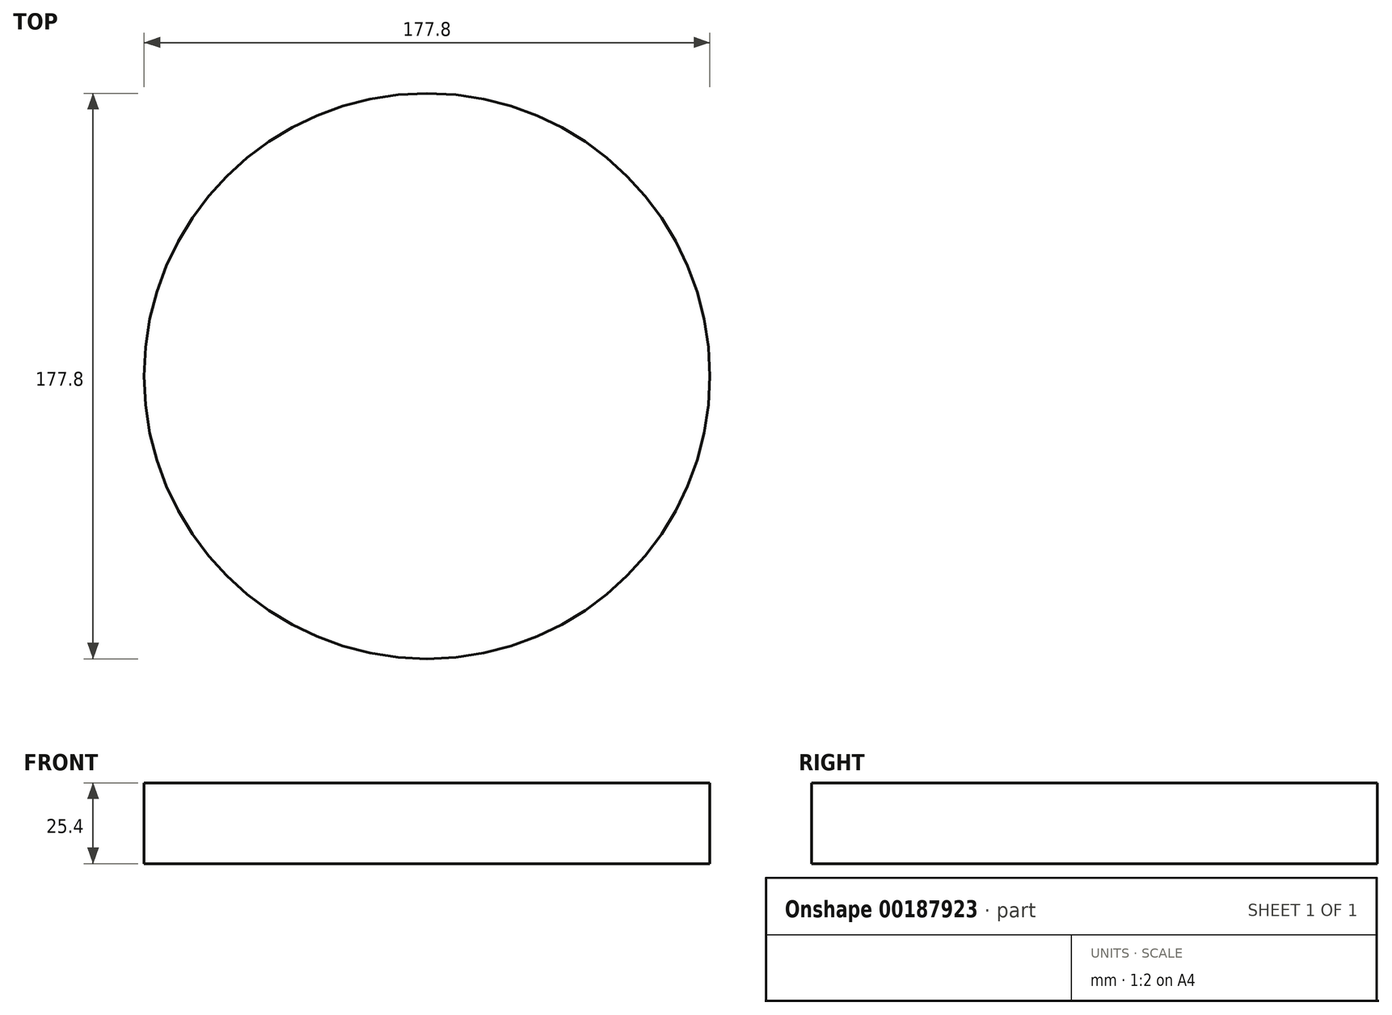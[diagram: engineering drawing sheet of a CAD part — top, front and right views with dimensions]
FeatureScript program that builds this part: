
annotation { "Feature Type Name" : "Feature", "Feature Type Description" : "" }
export const myFeature = defineFeature(function(context is Context, id is Id, definition is map)
    precondition{}
    {
        {
            var Q0;
            Q0=qCreatedBy(makeId("Top.planeOp"),FACE);
            var sketch = newSketch(context, id + "F0", { "sketchPlane" : qUnion([Q0])});
            skCircle(sketch, "E0", {"center": v(0, 0) * mm, "radius": 88.9 * mm});
            skSolve(sketch);
        }
        {
            var Q0;
            Q0 = qSketchRegion(id + "F0", true);
            extrude(context, id + "F1", {"entities" : qUnion([Q0]), "depth" : 25.4 * mm});
        }
    });
